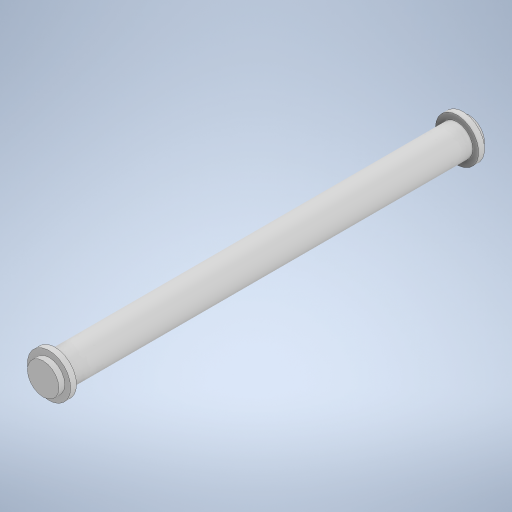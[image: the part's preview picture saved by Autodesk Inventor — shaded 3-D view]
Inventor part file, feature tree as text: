
AUTODESK INVENTOR PART (.ipt)
format: ipt  version: 2023 (Build 270158000, 158)  size: 256,512 bytes
history: native  units: in
note: dims shown in document units (in); Inventor stores cm internally (conversion verified against a paired STEP export)
features: extrude x5, sketch x5
ambient origin geometry x8: Origin, YZ Plane, XZ Plane, XY Plane, X Axis, Y Axis, Z Axis, Center Point
bodies: Solid1 (feature_tree)
feature tree (10):
  extrude  "Extrusion1"  Depth=102.2205in TaperAngle=0.0deg
  extrude  "Extrusion2"  Depth=1.5in TaperAngle=0.0deg
  extrude  "Extrusion3"  Depth=1.5in TaperAngle=0.0deg
  extrude  "Extrusion4"  Depth=1.5in
  extrude  "Extrusion5"  Depth=0.5in
  sketch  "Sketch1"  dims[d0=8.0in d1=102.2205in d2=0.0in]
  sketch  "Sketch2"  dims[d3=11.0in d4=1.5in d5=0.0in]
  sketch  "Sketch3"  dims[d6=1.5in d7=0.0in d8=1.5in d9=0.0in]
  sketch  "Sketch4"  dims[d10=1.5in d11=0.0in d12=0.5in]
  sketch  "Sketch5"  dims[d13=0.0344in d14=0.5in d15=0.0344in]
